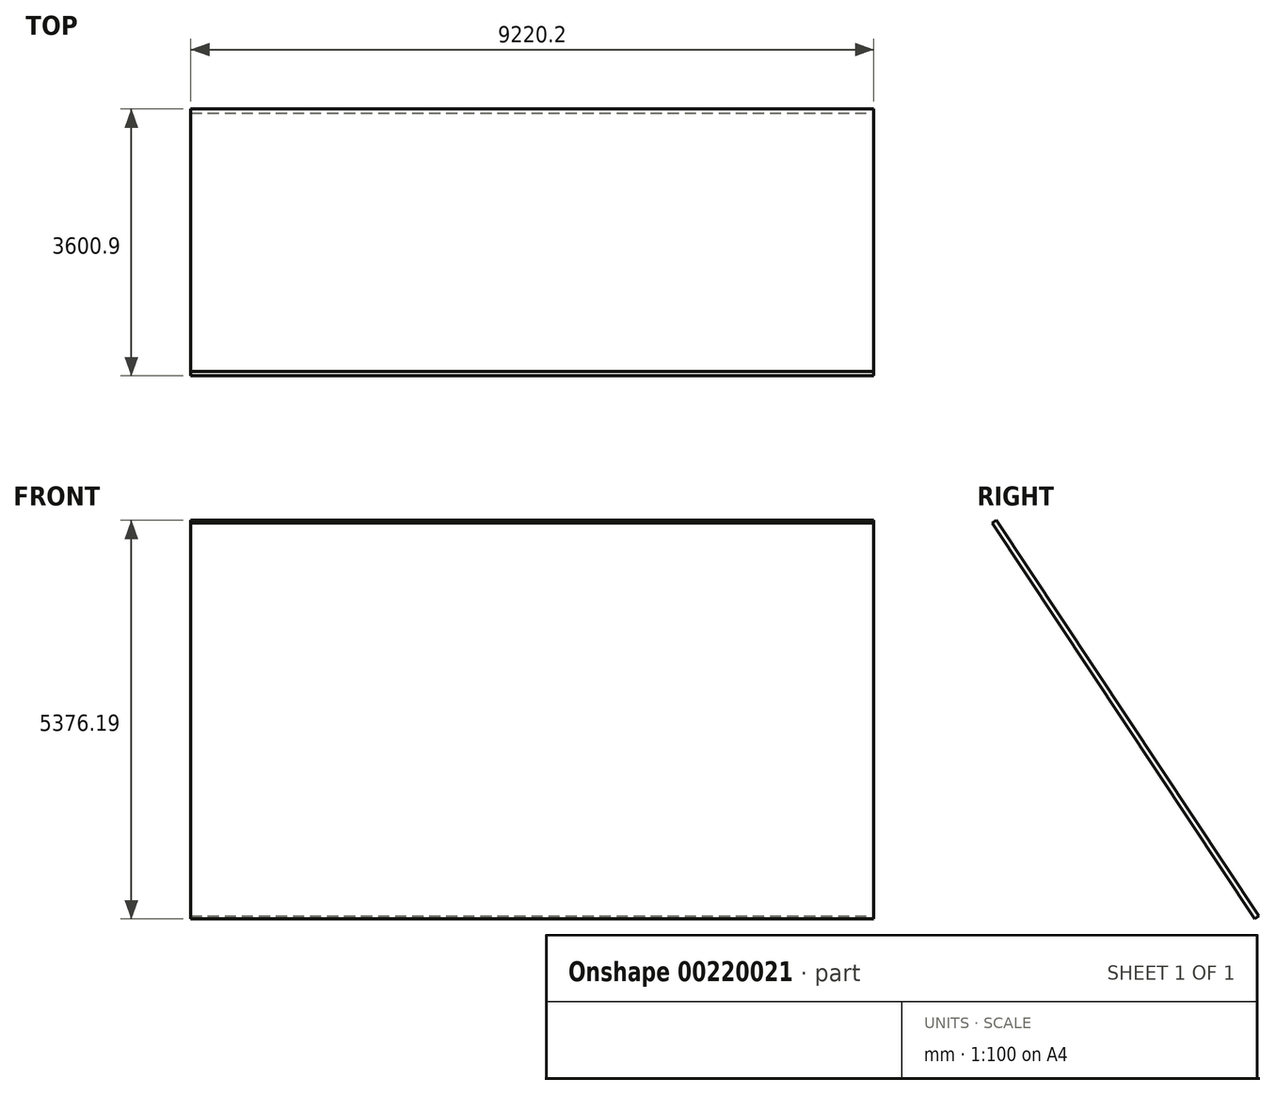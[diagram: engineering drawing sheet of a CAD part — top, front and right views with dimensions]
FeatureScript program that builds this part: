
annotation { "Feature Type Name" : "Feature", "Feature Type Description" : "" }
export const myFeature = defineFeature(function(context is Context, id is Id, definition is map)
    precondition{}
    {
        {
            var Q0;
            Q0=qCreatedBy(makeId("Right.planeOp"),FACE);
            var sketch = newSketch(context, id + "F0", { "sketchPlane" : qUnion([Q0])});
            skLineSegment(sketch, "E0", {"start": v(2933.7, 6096) * mm, "end": v(3543.3, 5177.64) * mm});
            skLineSegment(sketch, "E1", {"start": v(2933.7, 6096) * mm, "end": v(0, 10515.6) * mm});
            skSolve(sketch);
        }
        {
            var Q0;
            Q0=sQuery(id+"F0.wireOp",EDGE,"E1");
            var Q1;
            Q1=sQuery(id+"F0.wireOp",EDGE,"E0");
            extrude(context, id + "F1", {"bodyType" : ToolBodyType.SURFACE, "surfaceEntities" : qUnion([Q0, Q1]), "endBound" : BoundingType.SYMMETRIC, "depth" : 9220.2 * mm});
        }
        {
            var Q0;
            Q0=makeQuery(id+"F1.opExtrude","SWEPT_FACE",FACE,{"disambiguationData":[OSD([sQuery(id+"F0.wireOp",EDGE,"paPBDd7v-Khaj-EFFU-Sq9n-Kob8jBGrBa6K"),sQuery(id+"F0.wireOp",EDGE,"E0")])]});
            extrude(context, id + "F2", {"entities" : qUnion([Q0]), "depth" : 69.14 * mm});
        }
    });
